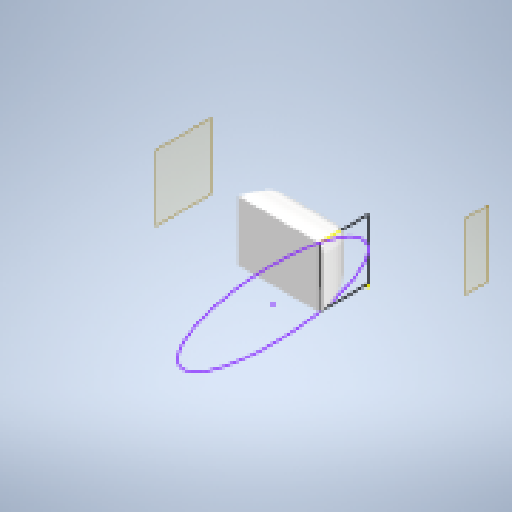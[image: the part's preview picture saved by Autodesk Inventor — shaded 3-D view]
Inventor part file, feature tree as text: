
AUTODESK INVENTOR PART (.ipt)
format: ipt  version: 2025.2 (Build 292293000, 293)  size: 443,904 bytes
history: native  units: in
note: dims shown in document units (in); Inventor stores cm internally (conversion verified against a paired STEP export)
features: reference x18, other x7, extrude x6, sketch x5, fillet x2, projected_geometry x2
ambient origin geometry x8: Origin, YZ Plane, XZ Plane, XY Plane, X Axis, Y Axis, Z Axis, Center Point
bodies: Body1 (feature_tree), Body2 (feature_tree), Body3 (feature_tree), Body4 (feature_tree)
feature tree (40):
  other  "ソリッド1"
  extrude  "押し出し1"  Depth=0.7874in TaperAngle=0.0deg
  extrude  "押し出し2"  TaperAngle=0.0deg  [1 undecoded]
  other  "作業平面3"
  sketch  "スケッチ5"
  extrude  "押し出し3"  Depth=3.937in TaperAngle=0.0deg
  extrude  "押し出し4"  Depth=3.937in TaperAngle=0.0deg
  extrude  "押し出し5"  Depth=3.937in TaperAngle=0.0deg
  fillet  "フィレット1"  Radius=0.1575in
  fillet  "フィレット2"  Radius=0.1181in
  other  "作業平面4"
  extrude  "押し出し6"  TaperAngle=90.0deg  [1 undecoded]
  sketch  "スケッチ1"
  reference  "参照1"
  reference  "参照3"
  reference  "参照4"
  reference  "参照5"
  reference  "参照6"
  reference  "参照7"
  reference  "参照8"
  reference  "参照9"
  reference  "参照10"
  reference  "参照11"
  reference  "参照12"
  reference  "参照13"
  reference  "参照14"
  reference  "参照15"
  sketch  "スケッチ2"
  reference  "参照16"
  reference  "参照17"
  reference  "参照18"
  reference  "参照19"
  sketch  "スケッチ6"
  projected_geometry  "投影ループ1"
  projected_geometry  "投影ループ2"
  sketch  "スケッチ9"
  other  "<userpath>\OneDrive\ドキュメント\New Controller\Hardware\Assembly.iam"
  other  "Assembly.iam"
  other  "Body_compleat01:1"
  other  "Body_compleat02:1"
note: 2 required parameter values undecoded (feature->parameter linkage not recoverable at this tier; creation-order binding heuristic only, values carry confidence <= 0.55)
